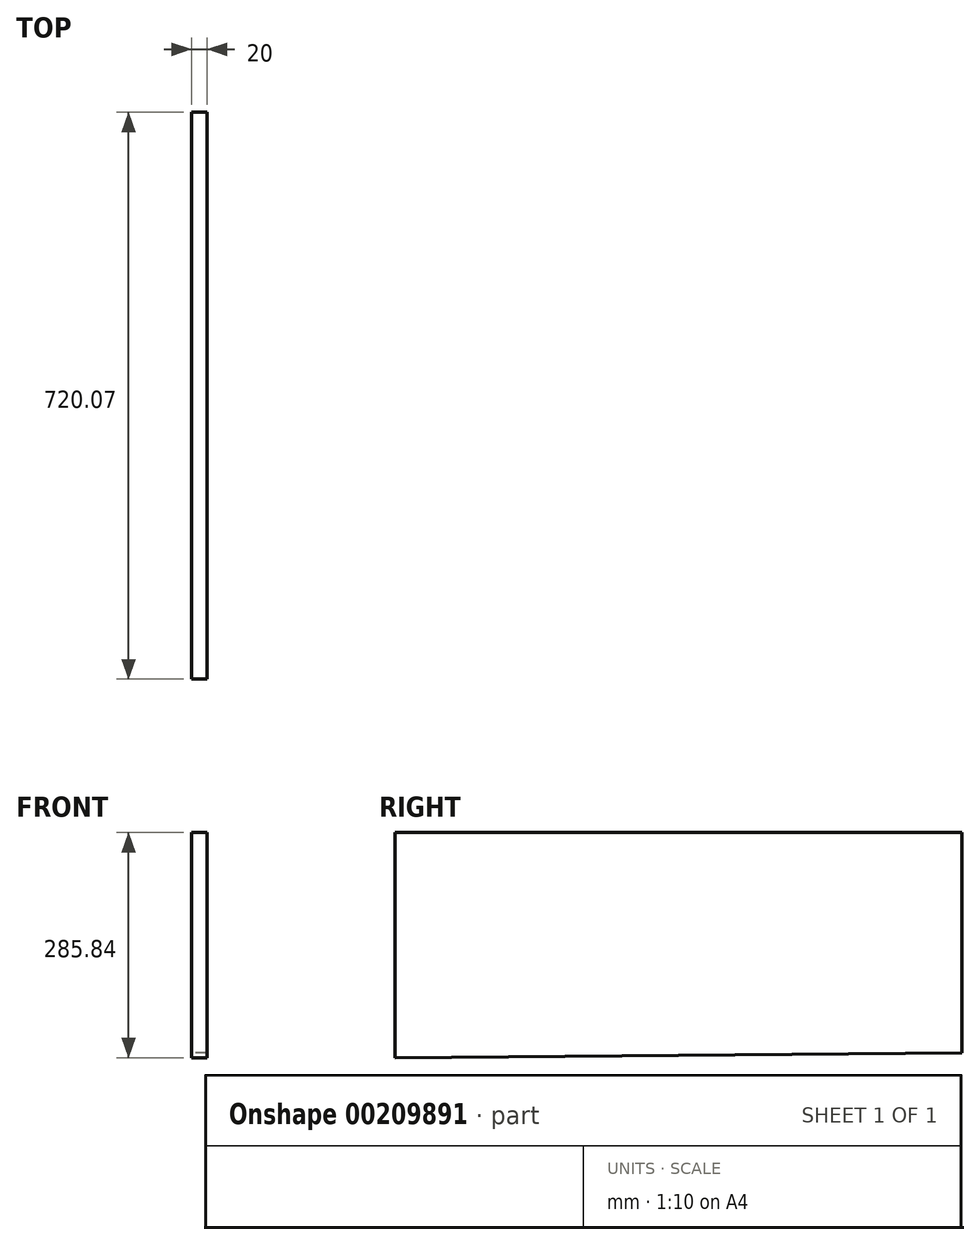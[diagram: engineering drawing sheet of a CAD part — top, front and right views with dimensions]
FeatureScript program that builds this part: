
annotation { "Feature Type Name" : "Feature", "Feature Type Description" : "" }
export const myFeature = defineFeature(function(context is Context, id is Id, definition is map)
    precondition{}
    {
        {
            var Q0;
            Q0=qCreatedBy(makeId("Right.planeOp"),FACE);
            var sketch = newSketch(context, id + "F0", { "sketchPlane" : qUnion([Q0])});
            skLineSegment(sketch, "E0", {"start": v(106.16, -104.7) * mm, "end": v(106.16, 175.35) * mm});
            skLineSegment(sketch, "E1", {"start": v(106.16, 175.35) * mm, "end": v(-613.91, 175.35) * mm});
            skLineSegment(sketch, "E2", {"start": v(-613.91, 175.35) * mm, "end": v(-613.91, -110.49) * mm});
            skLineSegment(sketch, "E3", {"start": v(-613.91, -110.49) * mm, "end": v(106.16, -104.7) * mm});
            skSolve(sketch);
        }
        {
            var Q0;
            Q0=makeQuery(id+"F0.imprint","IMPRINT",FACE,{"disambiguationData":[TD([[makeQuery(id+"F0.imprint","IMPRINT",EDGE,{"derivedFrom":sQuery(id+"F0.wireOp",EDGE,"E0")}),1.0]])]});
            extrude(context, id + "F1", {"entities" : qUnion([Q0]), "depth" : 20 * mm});
        }
    });
